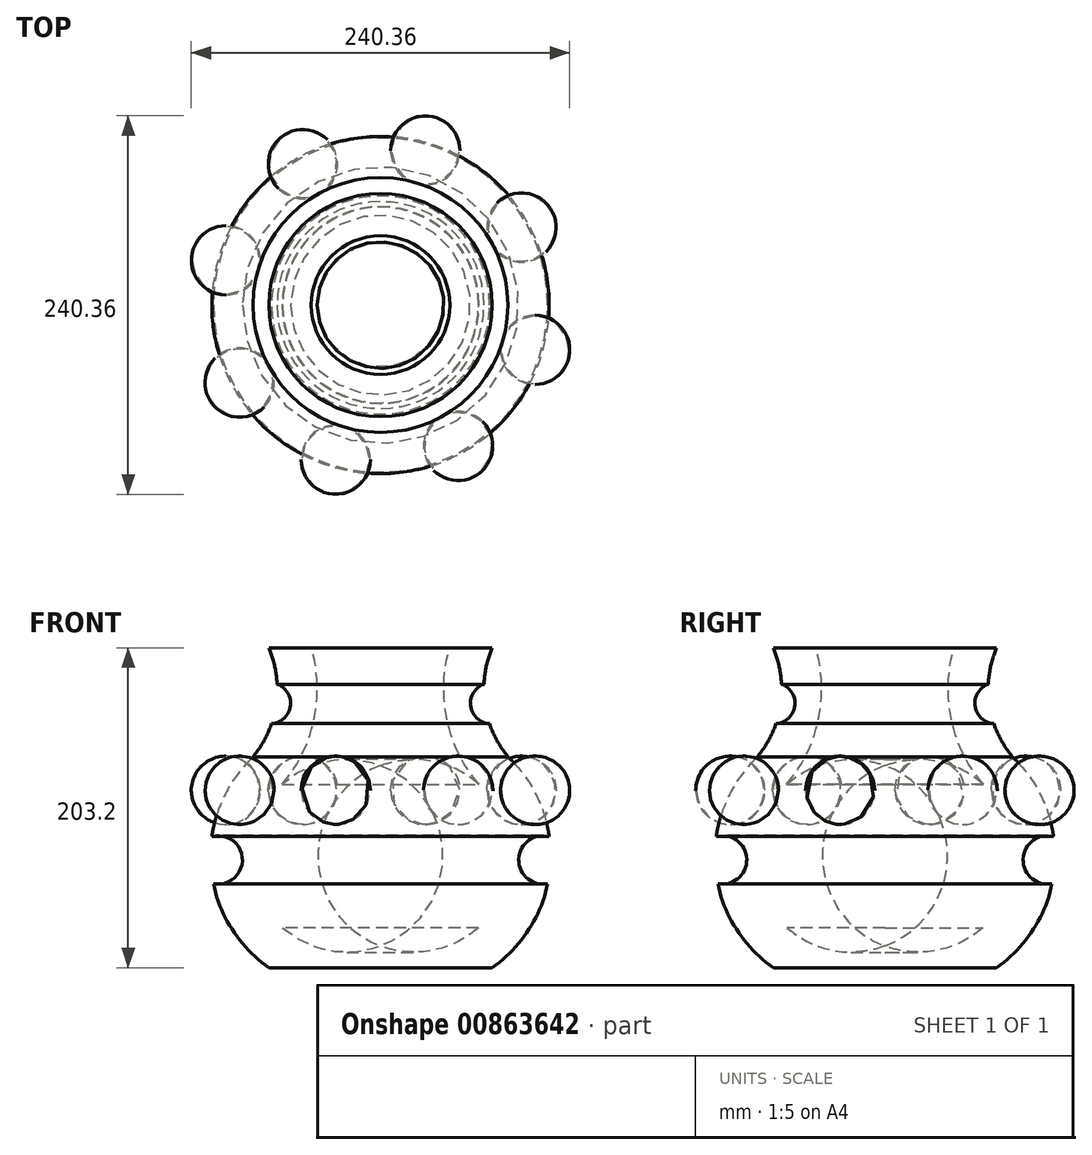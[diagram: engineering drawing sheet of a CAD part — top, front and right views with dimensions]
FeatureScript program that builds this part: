
annotation { "Feature Type Name" : "Feature", "Feature Type Description" : "" }
export const myFeature = defineFeature(function(context is Context, id is Id, definition is map)
    precondition{}
    {
        {
            var Q0;
            Q0=qCreatedBy(makeId("Front.planeOp"),FACE);
            var sketch = newSketch(context, id + "F0", { "sketchPlane" : qUnion([Q0])});
            skLineSegment(sketch, "E0", {"start": v(0, 0) * mm, "end": v(0, 203.2) * mm});
            skLineSegment(sketch, "E1", {"start": v(0, 203.2) * mm, "end": v(70.9, 203.2) * mm});
            skLineSegment(sketch, "E2", {"start": v(70.9, 0) * mm, "end": v(0, 0) * mm});
            skArc(sketch, "E3", {"start": v(70.9, 203.2) * mm, "mid": v(66.3, 167.2) * mm, "end": v(80.91, 133.96) * mm});
            skArc(sketch, "E4", {"start": v(70.9, 0) * mm, "mid": v(107.76, 64.6) * mm, "end": v(80.91, 133.96) * mm});
            skSolve(sketch);
        }
        {
            var Q0;
            Q0=makeQuery(id+"F0.imprint","IMPRINT",FACE,{"disambiguationData":[TD([[makeQuery(id+"F0.imprint","IMPRINT",EDGE,{"derivedFrom":sQuery(id+"F0.wireOp",EDGE,"E0")}),-1.0]])]});
            var Q1;
            Q1=sQuery(id+"F0.wireOp",EDGE,"E0");
            revolve(context, id + "F1", {"surfaceOperationType" : NewSurfaceOperationType.NEW, "entities" : qUnion([Q0]), "axis" : qUnion([Q1]), "revolveType" : RevolveType.FULL});
        }
        {
            var Q0;
            Q0=qCreatedBy(makeId("Front.planeOp"),FACE);
            var sketch = newSketch(context, id + "F2", { "sketchPlane" : qUnion([Q0])});
            skArc(sketch, "E5", {"start": v(-46.75, -0.79) * mm, "mid": v(-67.86, -22.85) * mm, "end": v(-46.04, -44.21) * mm});
            skLineSegment(sketch, "E6", {"start": v(-46.75, -0.79) * mm, "end": v(-46.04, -44.21) * mm});
            skSolve(sketch);
        }
        {
            var Q0;
            Q0=makeQuery(id+"F2.imprint","IMPRINT",FACE,{"disambiguationData":[TD([[makeQuery(id+"F2.imprint","IMPRINT",EDGE,{"derivedFrom":sQuery(id+"F2.wireOp",EDGE,"E5")}),1.0]])]});
            var Q1;
            Q1=sQuery(id+"F2.wireOp",EDGE,"E6");
            revolve(context, id + "F3", {"surfaceOperationType" : NewSurfaceOperationType.NEW, "entities" : qUnion([Q0]), "axis" : qUnion([Q1]), "revolveType" : RevolveType.FULL});
        }
        {
            var Q0;
            Q0=makeQuery(id+"F3.opRevolve","SWEPT_BODY",BODY,{"disambiguationData":[OSD([sQuery(id+"F2.wireOp",EDGE,"E5"),sQuery(id+"F2.wireOp",EDGE,"E6")])]});
            transform(context, id + "F4", {"entities" : qUnion([Q0]), "transformType" : TransformType.TRANSLATION_3D, "dx" : -51.82 * mm, "dy" : 28.45 * mm, "dz" : 135.13 * mm, "makeCopy" : false});
        }
        {
            var Q0;
            Q0=makeQuery(id+"F3.opRevolve","SWEPT_BODY",BODY,{"disambiguationData":[OSD([sQuery(id+"F2.wireOp",EDGE,"E5"),sQuery(id+"F2.wireOp",EDGE,"E6")])]});
            var Q1;
            Q1=makeQuery(id+"F1.opRevolve","SWEPT_EDGE",EDGE,{"disambiguationData":[OSD([sQuery(id+"F0.wireOp",EDGE,"E1"),sQuery(id+"F0.wireOp",EDGE,"E3")])]});
            circularPattern(context, id + "F5", {"entities" : qUnion([Q0]), "axis" : qUnion([Q1]), "angle" : 360 * degree, "instanceCount" : 8, "equalSpace" : true});
        }
        {
            var Q0;
            Q0=makeQuery(id+"F1.opRevolve","SWEPT_FACE",FACE,{"disambiguationData":[OSD([sQuery(id+"F0.wireOp",EDGE,"E1")])]});
            shell(context, id + "F6", {"entities" : qUnion([Q0]), "thickness" : 25.4 * mm});
        }
        {
            var Q0;
            Q0=qCreatedBy(makeId("Front.planeOp"),FACE);
            var sketch = newSketch(context, id + "F7", { "sketchPlane" : qUnion([Q0])});
            skCircle(sketch, "E7", {"center": v(69.93, 167.87) * mm, "radius": 12.86 * mm});
            skSolve(sketch);
        }
        {
            var Q0;
            Q0=makeQuery(id+"F7.imprint","IMPRINT",FACE,{"disambiguationData":[TD([[makeQuery(id+"F7.imprint","IMPRINT",EDGE,{"derivedFrom":sQuery(id+"F7.wireOp",EDGE,"E7")}),1.0]])]});
            var Q1;
            Q1=makeQuery(id+"F1.opRevolve","SWEPT_FACE",FACE,{"disambiguationData":[OSD([sQuery(id+"F0.wireOp",EDGE,"E3")])]});
            revolve(context, id + "F8", {"operationType" : NewBodyOperationType.REMOVE, "surfaceOperationType" : NewSurfaceOperationType.NEW, "entities" : qUnion([Q0]), "axis" : qUnion([Q1]), "revolveType" : RevolveType.FULL, "oppositeDirection" : true});
        }
        {
            var Q0;
            Q0=qCreatedBy(makeId("Front.planeOp"),FACE);
            var sketch = newSketch(context, id + "F9", { "sketchPlane" : qUnion([Q0])});
            skCircle(sketch, "E8", {"center": v(-103.15, 68.45) * mm, "radius": 15.41 * mm});
            skSolve(sketch);
        }
        {
            var Q0;
            Q0=makeQuery(id+"F9.imprint","IMPRINT",FACE,{"disambiguationData":[TD([[makeQuery(id+"F9.imprint","IMPRINT",EDGE,{"derivedFrom":sQuery(id+"F9.wireOp",EDGE,"E8")}),1.0]])]});
            var Q1;
            Q1=makeQuery(id+"F1.opRevolve","SWEPT_FACE",FACE,{"disambiguationData":[OSD([sQuery(id+"F0.wireOp",EDGE,"E4")])]});
            revolve(context, id + "F10", {"operationType" : NewBodyOperationType.REMOVE, "surfaceOperationType" : NewSurfaceOperationType.NEW, "entities" : qUnion([Q0]), "axis" : qUnion([Q1]), "revolveType" : RevolveType.FULL, "oppositeDirection" : true});
        }
        {
            var Q0;
            Q0=qCreatedBy(makeId("Front.planeOp"),FACE);
            var sketch = newSketch(context, id + "F11", { "sketchPlane" : qUnion([Q0])});
            skArc(sketch, "E9", {"start": v(-141.06, 32.18) * mm, "mid": v(-154.9, 14.22) * mm, "end": v(-137.05, 0.23) * mm});
            skLineSegment(sketch, "E10", {"start": v(-141.06, 32.18) * mm, "end": v(-137.05, 0.23) * mm});
            skSolve(sketch);
        }
        {
            var Q0;
            Q0=makeQuery(id+"F11.imprint","IMPRINT",FACE,{"disambiguationData":[TD([[makeQuery(id+"F11.imprint","IMPRINT",EDGE,{"derivedFrom":sQuery(id+"F11.wireOp",EDGE,"E9")}),1.0]])]});
            var Q1;
            Q1=sQuery(id+"F11.wireOp",EDGE,"E10");
            revolve(context, id + "F12", {"surfaceOperationType" : NewSurfaceOperationType.NEW, "entities" : qUnion([Q0]), "axis" : qUnion([Q1]), "revolveType" : RevolveType.FULL});
        }
        {
            var Q0;
            Q0=makeQuery(id+"F12.opRevolve","SWEPT_BODY",BODY,{"disambiguationData":[OSD([sQuery(id+"F11.wireOp",EDGE,"E9"),sQuery(id+"F11.wireOp",EDGE,"E10")])]});
            transform(context, id + "F13", {"entities" : qUnion([Q0]), "transformType" : TransformType.TRANSLATION_3D, "dx" : 80.77 * mm, "dy" : 0 * mm, "dz" : 178.56 * mm, "makeCopy" : false});
        }
        {
            var Q0;
            Q0=makeQuery(id+"F12.opRevolve","SWEPT_BODY",BODY,{"disambiguationData":[OSD([sQuery(id+"F11.wireOp",EDGE,"E9"),sQuery(id+"F11.wireOp",EDGE,"E10")])]});
            var Q1;
            Q1=makeQuery(id+"F1.opRevolve","SWEPT_EDGE",EDGE,{"disambiguationData":[OSD([sQuery(id+"F0.wireOp",EDGE,"E1"),sQuery(id+"F0.wireOp",EDGE,"E3")])]});
            circularPattern(context, id + "F14", {"entities" : qUnion([Q0]), "axis" : qUnion([Q1]), "angle" : 360 * degree, "instanceCount" : 6, "equalSpace" : true});
        }
        {
            var Q0;
            Q0=makeQuery(id+"F14.opPattern","COPY",BODY,{"derivedFrom":makeQuery(id+"F12.opRevolve","SWEPT_BODY",BODY,{"disambiguationData":[OSD([sQuery(id+"F11.wireOp",EDGE,"E9"),sQuery(id+"F11.wireOp",EDGE,"E10")])]}),"instanceName":"4"});
            var Q1;
            Q1=makeQuery(id+"F14.opPattern","COPY",BODY,{"derivedFrom":makeQuery(id+"F12.opRevolve","SWEPT_BODY",BODY,{"disambiguationData":[OSD([sQuery(id+"F11.wireOp",EDGE,"E9"),sQuery(id+"F11.wireOp",EDGE,"E10")])]}),"instanceName":"5"});
            var Q2;
            Q2=makeQuery(id+"F14.opPattern","COPY",BODY,{"derivedFrom":makeQuery(id+"F12.opRevolve","SWEPT_BODY",BODY,{"disambiguationData":[OSD([sQuery(id+"F11.wireOp",EDGE,"E9"),sQuery(id+"F11.wireOp",EDGE,"E10")])]}),"instanceName":"3"});
            var Q3;
            Q3=makeQuery(id+"F14.opPattern","COPY",BODY,{"derivedFrom":makeQuery(id+"F12.opRevolve","SWEPT_BODY",BODY,{"disambiguationData":[OSD([sQuery(id+"F11.wireOp",EDGE,"E9"),sQuery(id+"F11.wireOp",EDGE,"E10")])]}),"instanceName":"2"});
            var Q4;
            Q4=makeQuery(id+"F12.opRevolve","SWEPT_BODY",BODY,{"disambiguationData":[OSD([sQuery(id+"F11.wireOp",EDGE,"E9"),sQuery(id+"F11.wireOp",EDGE,"E10")])]});
            var Q5;
            Q5=makeQuery(id+"F14.opPattern","COPY",BODY,{"derivedFrom":makeQuery(id+"F12.opRevolve","SWEPT_BODY",BODY,{"disambiguationData":[OSD([sQuery(id+"F11.wireOp",EDGE,"E9"),sQuery(id+"F11.wireOp",EDGE,"E10")])]}),"instanceName":"1"});
            var Q6;
            Q6=makeQuery(id+"F5.opPattern","COPY",BODY,{"derivedFrom":makeQuery(id+"F3.opRevolve","SWEPT_BODY",BODY,{"disambiguationData":[OSD([sQuery(id+"F2.wireOp",EDGE,"E5"),sQuery(id+"F2.wireOp",EDGE,"E6")])]}),"instanceName":"7"});
            booleanBodies(context, id + "F15", {"operationType" : BooleanOperationType.SUBTRACTION, "tools" : qUnion([Q0, Q1, Q2, Q3, Q4, Q5]), "targets" : qUnion([Q6])});
        }
    });
